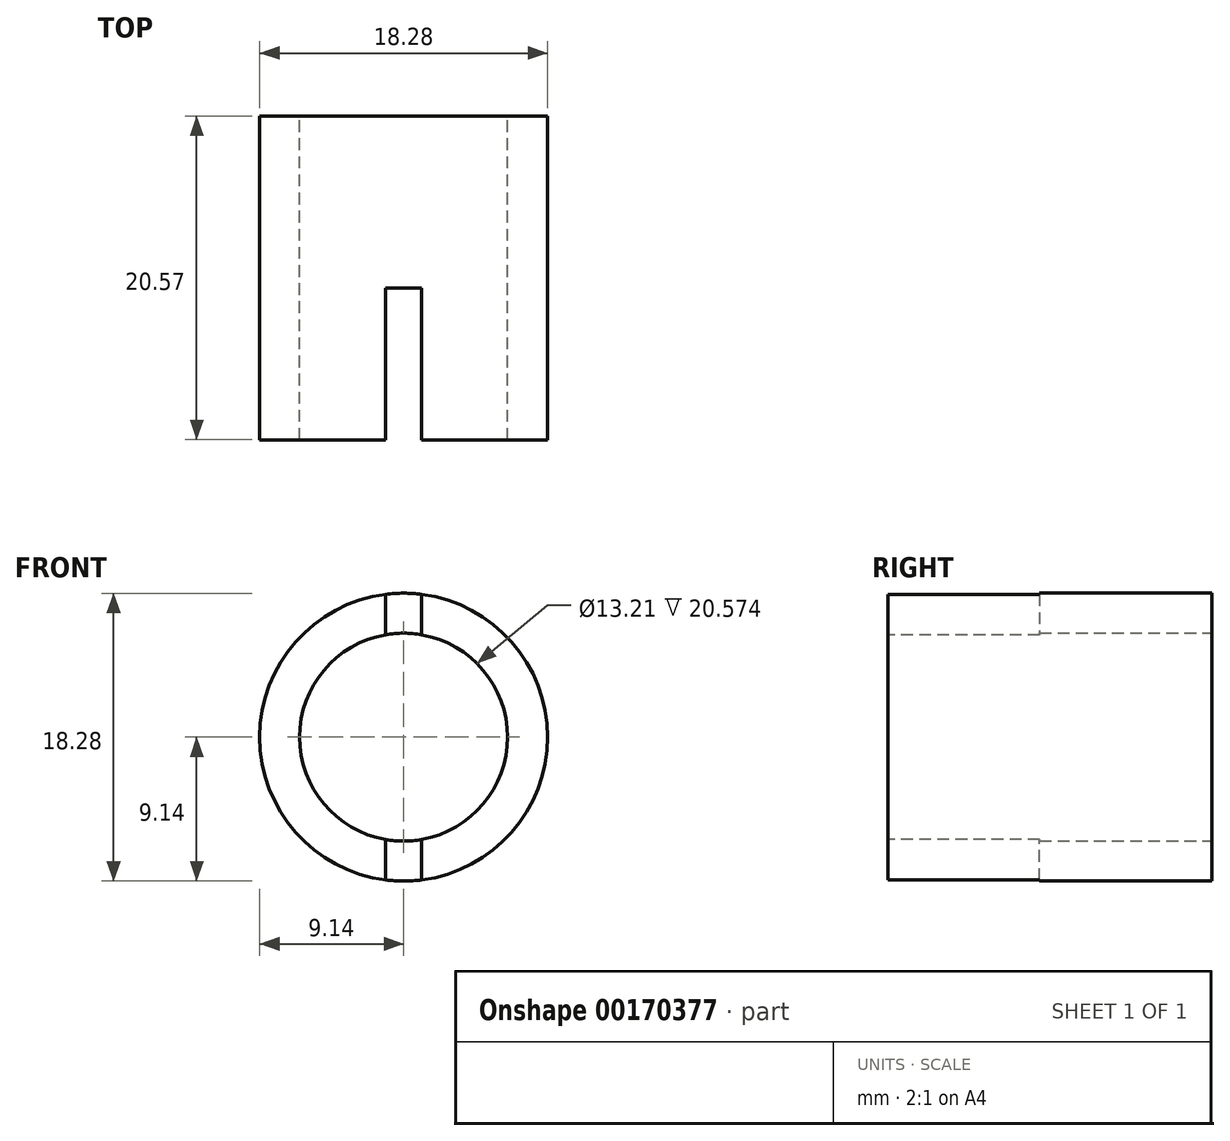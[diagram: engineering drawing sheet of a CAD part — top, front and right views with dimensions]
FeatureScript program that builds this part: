
annotation { "Feature Type Name" : "Feature", "Feature Type Description" : "" }
export const myFeature = defineFeature(function(context is Context, id is Id, definition is map)
    precondition{}
    {
        {
            var Q0;
            Q0=qCreatedBy(makeId("Front.planeOp"),FACE);
            var sketch = newSketch(context, id + "F0", { "sketchPlane" : qUnion([Q0])});
            skCircle(sketch, "E0", {"center": v(0, 0) * mm, "radius": 9.14 * mm});
            skCircle(sketch, "E1", {"center": v(0, 0) * mm, "radius": 6.6 * mm});
            skSolve(sketch);
        }
        {
            var Q0;
            Q0=makeQuery(id+"F0.imprint","IMPRINT",FACE,{"disambiguationData":[TD([[makeQuery(id+"F0.imprint","IMPRINT",EDGE,{"derivedFrom":sQuery(id+"F0.wireOp",EDGE,"E0")}),1.0]])]});
            extrude(context, id + "F1", {"entities" : qUnion([Q0]), "depth" : 10.92 * mm});
        }
        {
            var Q0;
            Q0=qCreatedBy(makeId("Front.planeOp"),FACE);
            cPlane(context, id + "F2", {"entities" : qUnion([Q0]), "cplaneType" : CPlaneType.OFFSET, "offset" : 20.57 * mm, "width" : 152.4 * mm, "height" : 152.4 * mm});
        }
        {
            var Q0;
            Q0=qCreatedBy(id+"F2.planeOp",FACE);
            var sketch = newSketch(context, id + "F3", { "sketchPlane" : qUnion([Q0])});
            skArc(sketch, "E2", {"start": v(-1.14, 9.07) * mm, "mid": v(-9.14, 0) * mm, "end": v(-1.14, -9.07) * mm});
            skArc(sketch, "E3", {"start": v(-1.14, 6.5) * mm, "mid": v(-6.6, 0) * mm, "end": v(-1.14, -6.5) * mm});
            skLineSegment(sketch, "E4", {"start": v(1.14, 9.07) * mm, "end": v(1.14, 6.5) * mm});
            skLineSegment(sketch, "E5", {"start": v(-1.14, 9.07) * mm, "end": v(-1.14, 6.5) * mm});
            skLineSegment(sketch, "E6", {"start": v(1.14, -9.07) * mm, "end": v(1.14, -6.5) * mm});
            skLineSegment(sketch, "E7", {"start": v(-1.14, -6.5) * mm, "end": v(-1.14, -9.07) * mm});
            skArc(sketch, "E8.trimOffspring", {"start": v(1.14, -9.07) * mm, "mid": v(9.14, 0) * mm, "end": v(1.14, 9.07) * mm});
            skArc(sketch, "E9.trimOffspring", {"start": v(1.14, -6.5) * mm, "mid": v(6.6, 0) * mm, "end": v(1.14, 6.5) * mm});
            skSolve(sketch);
        }
        {
            var Q0;
            Q0 = qSketchRegion(id + "F3", true);
            extrude(context, id + "F4", {"entities" : qUnion([Q0]), "operationType" : NewBodyOperationType.ADD, "oppositeDirection" : true, "depth" : 9.65 * mm});
        }
    });
